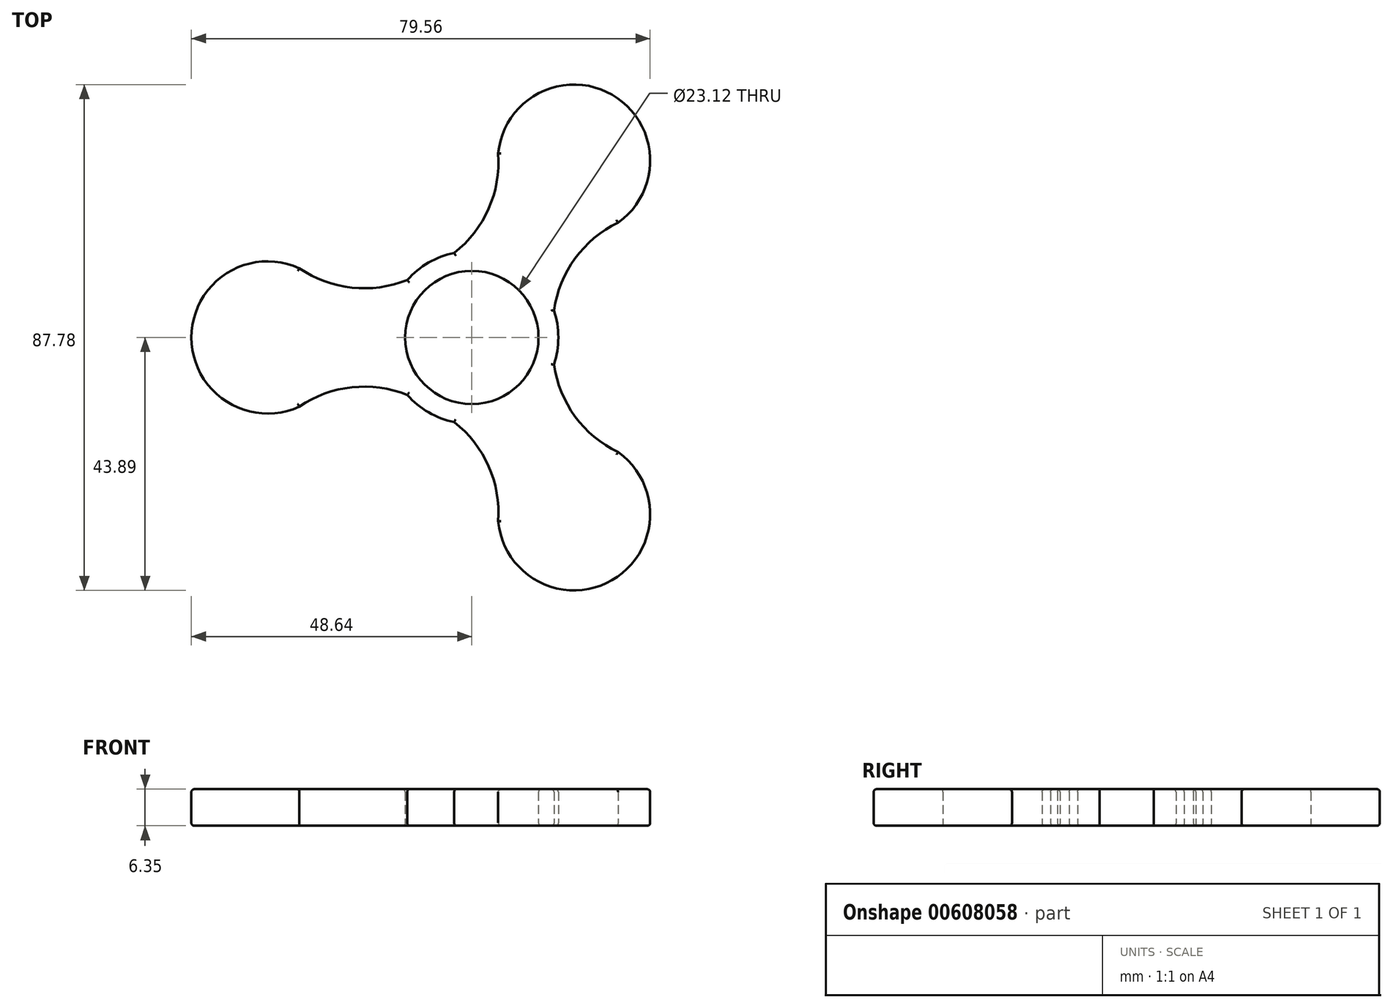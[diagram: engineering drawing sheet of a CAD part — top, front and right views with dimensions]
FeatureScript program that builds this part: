
annotation { "Feature Type Name" : "Feature", "Feature Type Description" : "" }
export const myFeature = defineFeature(function(context is Context, id is Id, definition is map)
    precondition{}
    {
        {
            var Q0;
            Q0=qCreatedBy(makeId("Top.planeOp"),FACE);
            var sketch = newSketch(context, id + "F0", { "sketchPlane" : qUnion([Q0])});
            skCircle(sketch, "E0", {"center": v(0, 0) * mm, "radius": 11.56 * mm});
            skCircle(sketch, "E1", {"center": v(0, 0) * mm, "radius": 15 * mm});
            skArc(sketch, "E2", {"start": v(-29.92, 12) * mm, "mid": v(-20.8, 8.65) * mm, "end": v(-11.2, 9.99) * mm});
            skArc(sketch, "E3.MirrorCS", {"start": v(-29.92, -12) * mm, "mid": v(-20.8, -8.65) * mm, "end": v(-11.2, -9.99) * mm});
            skArc(sketch, "E4", {"start": v(-29.92, 12) * mm, "mid": v(-48.64, 0) * mm, "end": v(-29.92, -12) * mm});
            skArc(sketch, "E5.1.0", {"start": v(4.57, -31.91) * mm, "mid": v(2.91, -22.35) * mm, "end": v(-3.05, -14.69) * mm});
            skArc(sketch, "E5.1.1", {"start": v(4.57, -31.91) * mm, "mid": v(24.32, -42.13) * mm, "end": v(25.35, -19.91) * mm});
            skArc(sketch, "E5.1.2", {"start": v(25.35, -19.91) * mm, "mid": v(17.9, -13.7) * mm, "end": v(14.24, -4.7) * mm});
            skArc(sketch, "E5.2.0", {"start": v(25.35, 19.91) * mm, "mid": v(17.9, 13.7) * mm, "end": v(14.24, 4.7) * mm});
            skArc(sketch, "E5.2.1", {"start": v(25.35, 19.91) * mm, "mid": v(24.32, 42.13) * mm, "end": v(4.57, 31.91) * mm});
            skArc(sketch, "E5.2.2", {"start": v(4.57, 31.91) * mm, "mid": v(2.91, 22.35) * mm, "end": v(-3.05, 14.69) * mm});
            skSolve(sketch);
        }
        {
            var Q0;
            {var subQ0=sQuery(id+"F0.wireOp",EDGE,"E2");Q0=makeQuery(id+"F0.imprint","IMPRINT",FACE,{"disambiguationData":[TD([[makeQuery(id+"F0.imprint","IMPRINT",EDGE,{"derivedFrom":subQ0}),-1.0]])]});}
            var Q1;
            {var subQ0=sQuery(id+"F0.wireOp",EDGE,"E5.2.0");Q1=makeQuery(id+"F0.imprint","IMPRINT",FACE,{"disambiguationData":[TD([[makeQuery(id+"F0.imprint","IMPRINT",EDGE,{"derivedFrom":subQ0}),-1.0]])]});}
            var Q2;
            Q2=makeQuery(id+"F0.imprint","IMPRINT",FACE,{"disambiguationData":[TD([[makeQuery(id+"F0.imprint","IMPRINT",EDGE,{"derivedFrom":sQuery(id+"F0.wireOp",EDGE,"E0")}),-1.0]])]});
            var Q3;
            {var subQ0=sQuery(id+"F0.wireOp",EDGE,"E5.1.0");Q3=makeQuery(id+"F0.imprint","IMPRINT",FACE,{"disambiguationData":[TD([[makeQuery(id+"F0.imprint","IMPRINT",EDGE,{"derivedFrom":subQ0}),-1.0]])]});}
            extrude(context, id + "F1", {"entities" : qUnion([Q0, Q1, Q2, Q3]), "depth" : 6.35 * mm, "offsetDistance" : 25 * mm});
        }
        {
            var Q0;
            Q0=makeQuery(id+"F1.opExtrude","CAP_FACE",FACE,{"disambiguationData":[OSD([sQuery(id+"F0.wireOp",EDGE,"E0"),sQuery(id+"F0.wireOp",EDGE,"E1"),sQuery(id+"F0.wireOp",EDGE,"E2"),sQuery(id+"F0.wireOp",EDGE,"E3.MirrorCS"),sQuery(id+"F0.wireOp",EDGE,"E4"),sQuery(id+"F0.wireOp",EDGE,"E5.1.0"),sQuery(id+"F0.wireOp",EDGE,"E5.1.1"),sQuery(id+"F0.wireOp",EDGE,"E5.1.2"),sQuery(id+"F0.wireOp",EDGE,"E5.2.0"),sQuery(id+"F0.wireOp",EDGE,"E5.2.1"),sQuery(id+"F0.wireOp",EDGE,"E5.2.2")])],"isStart":false});
            var Q1;
            Q1=makeQuery(id+"F1.opExtrude","CAP_FACE",FACE,{"disambiguationData":[OSD([sQuery(id+"F0.wireOp",EDGE,"E0"),sQuery(id+"F0.wireOp",EDGE,"E1"),sQuery(id+"F0.wireOp",EDGE,"E2"),sQuery(id+"F0.wireOp",EDGE,"E3.MirrorCS"),sQuery(id+"F0.wireOp",EDGE,"E4"),sQuery(id+"F0.wireOp",EDGE,"E5.1.0"),sQuery(id+"F0.wireOp",EDGE,"E5.1.1"),sQuery(id+"F0.wireOp",EDGE,"E5.1.2"),sQuery(id+"F0.wireOp",EDGE,"E5.2.0"),sQuery(id+"F0.wireOp",EDGE,"E5.2.1"),sQuery(id+"F0.wireOp",EDGE,"E5.2.2")])],"isStart":true});
            fillet(context, id + "F2", {"entities" : qUnion([Q0, Q1]), "radius" : .5 * mm, "tangentPropagation" : true, "allowEdgeOverflow" : false});
        }
    });
